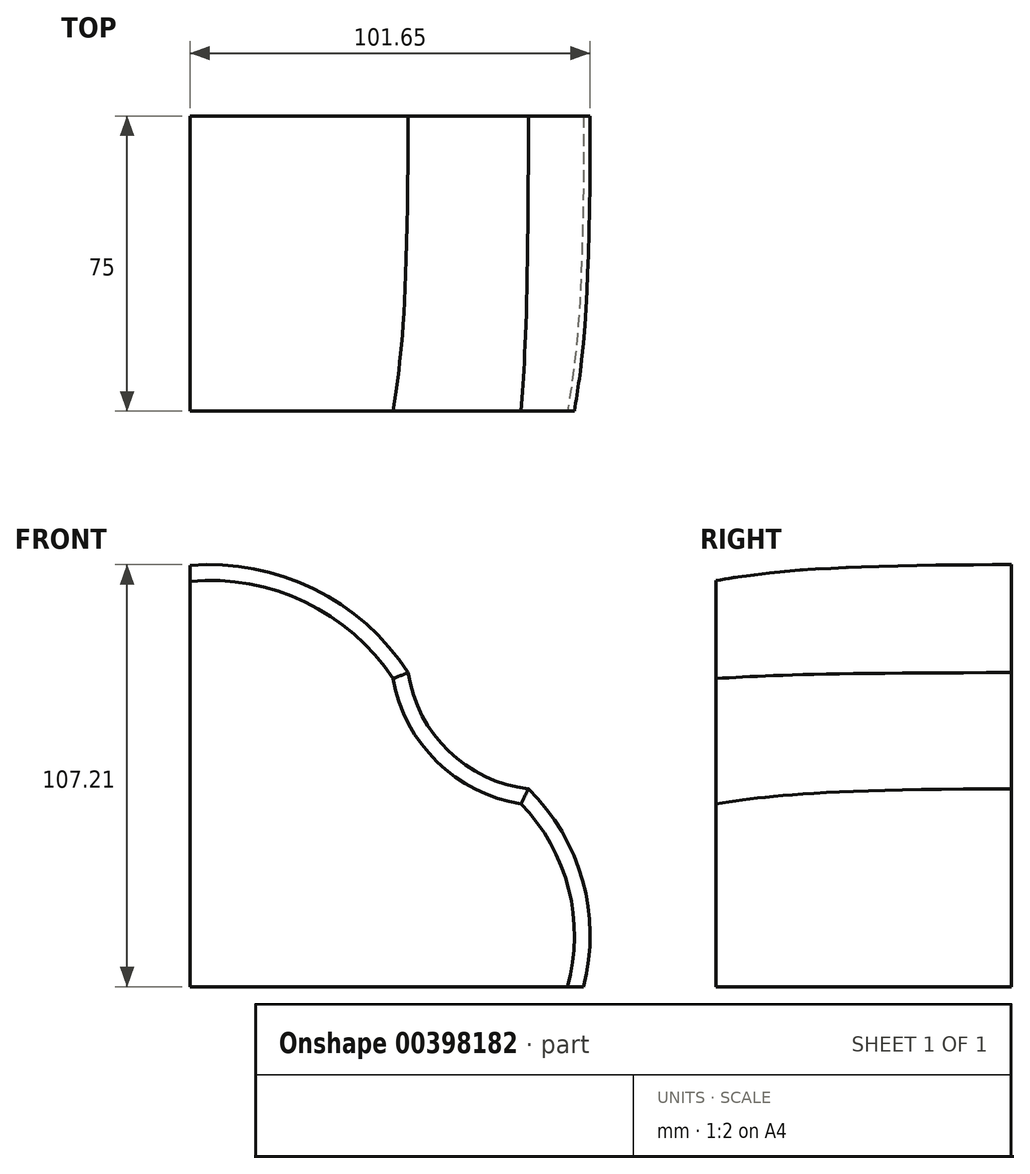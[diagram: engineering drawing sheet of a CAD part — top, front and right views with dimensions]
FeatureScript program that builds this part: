
annotation { "Feature Type Name" : "Feature", "Feature Type Description" : "" }
export const myFeature = defineFeature(function(context is Context, id is Id, definition is map)
    precondition{}
    {
        {
            var Q0;
            Q0=qCreatedBy(makeId("Front.planeOp"),FACE);
            cPlane(context, id + "F0", {"entities" : qUnion([Q0]), "cplaneType" : CPlaneType.OFFSET, "offset" : 75 * mm, "width" : 150 * mm, "height" : 150 * mm});
        }
        {
            var Q0;
            Q0=qCreatedBy(makeId("Front.planeOp"),FACE);
            var sketch = newSketch(context, id + "F1", { "sketchPlane" : qUnion([Q0])});
            skArc(sketch, "E0", {"start": v(55.4, 29.54) * mm, "mid": v(31.46, 50.82) * mm, "end": v(0, 56.76) * mm});
            skArc(sketch, "E1", {"start": v(55.4, 29.54) * mm, "mid": v(65.67, 9.6) * mm, "end": v(85.95, 0) * mm});
            skArc(sketch, "E2", {"start": v(100, -50.24) * mm, "mid": v(99.73, -23.23) * mm, "end": v(85.95, 0) * mm});
            skLineSegment(sketch, "E3", {"start": v(0, 56.76) * mm, "end": v(0, -50.24) * mm});
            skLineSegment(sketch, "E4", {"start": v(0, -50.24) * mm, "end": v(100, -50.24) * mm});
            skSolve(sketch);
        }
        {
            var Q0;
            Q0=qCreatedBy(id+"F0.planeOp",FACE);
            var sketch = newSketch(context, id + "F2", { "sketchPlane" : qUnion([Q0])});
            skArc(sketch, "E5.0", {"start": v(51.58, 28.06) * mm, "mid": v(29.18, 47.48) * mm, "end": v(0, 52.75) * mm});
            skArc(sketch, "E6.0", {"start": v(51.58, 28.06) * mm, "mid": v(62.7, 6.9) * mm, "end": v(84.07, -3.78) * mm});
            skArc(sketch, "E7.0", {"start": v(95.86, -50.24) * mm, "mid": v(96.18, -25.43) * mm, "end": v(84.07, -3.78) * mm});
            skLineSegment(sketch, "E8", {"start": v(0, -50.24) * mm, "end": v(95.86, -50.24) * mm});
            skLineSegment(sketch, "E9", {"start": v(0, 52.75) * mm, "end": v(0, -50.24) * mm});
            skSolve(sketch);
        }
        {
            var Q0;
            Q0=makeQuery(id+"F1.imprint","IMPRINT",FACE,{"disambiguationData":[TD([[makeQuery(id+"F1.imprint","IMPRINT",EDGE,{"derivedFrom":sQuery(id+"F1.wireOp",EDGE,"E0")}),1.0]])]});
            var Q1;
            Q1=makeQuery(id+"F2.imprint","IMPRINT",FACE,{"disambiguationData":[TD([[makeQuery(id+"F2.imprint","IMPRINT",EDGE,{"derivedFrom":sQuery(id+"F2.wireOp",EDGE,"E5.0")}),1.0]])]});
            loft(context, id + "F3", {"startCondition" : LoftEndDerivativeType.NORMAL_TO_PROFILE, "startMagnitude" : 2, "sheetProfilesArray" : [{ "sheetProfileEntities" : qUnion([Q0]) }, { "sheetProfileEntities" : qUnion([Q1]) }]});
        }
    });
